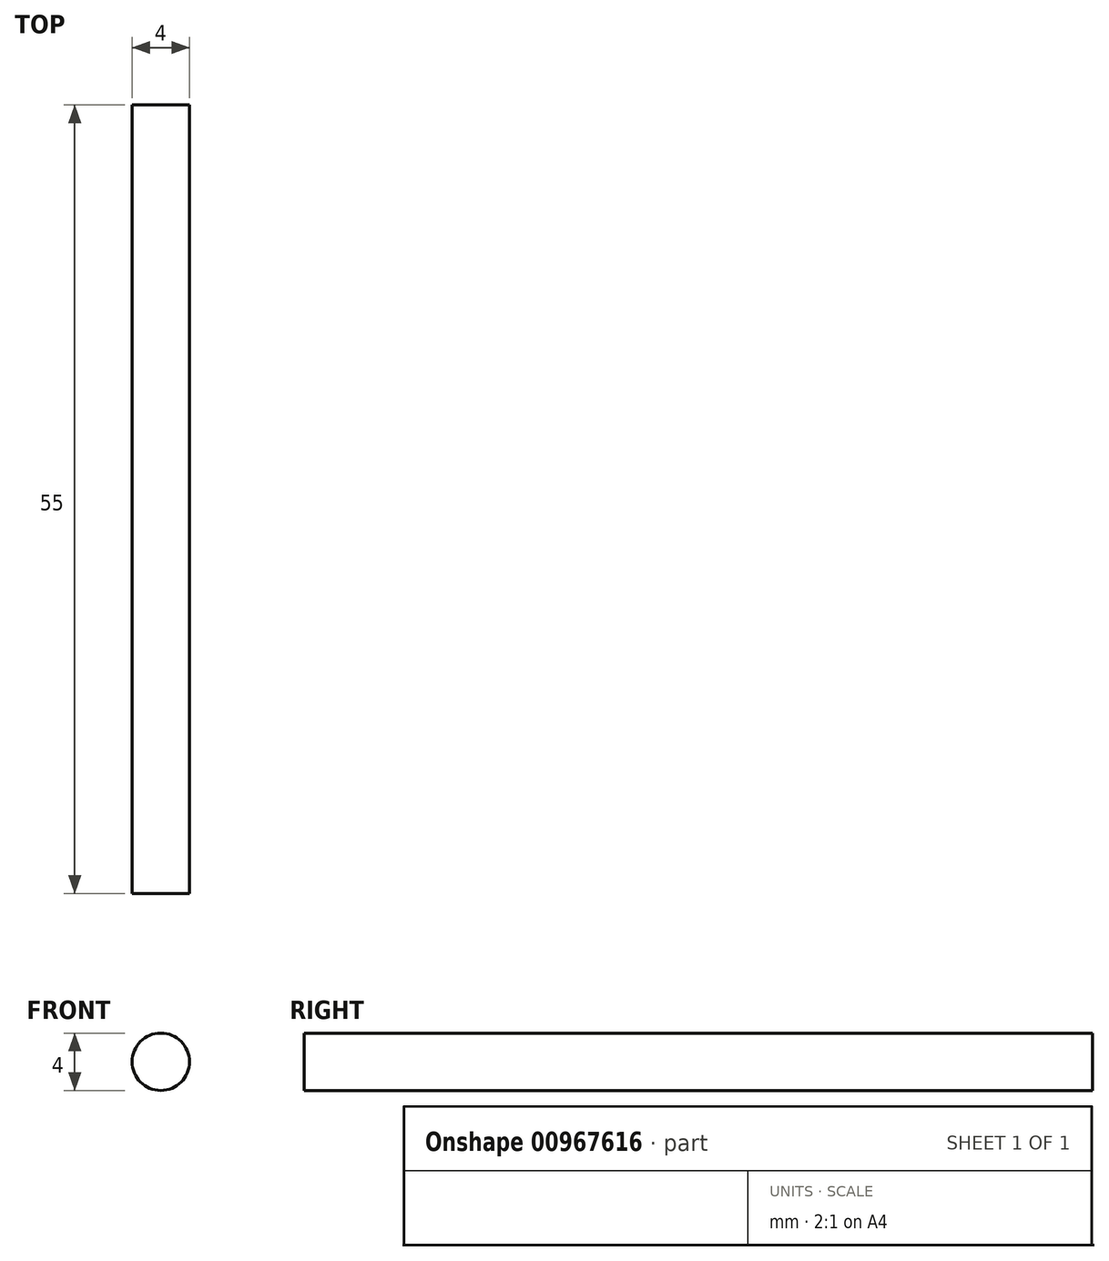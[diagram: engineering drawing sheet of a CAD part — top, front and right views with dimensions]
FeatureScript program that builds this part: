
annotation { "Feature Type Name" : "Feature", "Feature Type Description" : "" }
export const myFeature = defineFeature(function(context is Context, id is Id, definition is map)
    precondition{}
    {
        {
            var Q0;
            Q0=qCreatedBy(makeId("Front.planeOp"),FACE);
            var sketch = newSketch(context, id + "F0", { "sketchPlane" : qUnion([Q0])});
            skCircle(sketch, "E0", {"center": v(0, 0) * mm, "radius": 2 * mm});
            skSolve(sketch);
        }
        {
            var Q0;
            Q0 = qSketchRegion(id + "F0", true);
            extrude(context, id + "F1", {"entities" : qUnion([Q0]), "oppositeDirection" : true, "depth" : 55 * mm, "offsetDistance" : 25 * mm});
        }
    });
